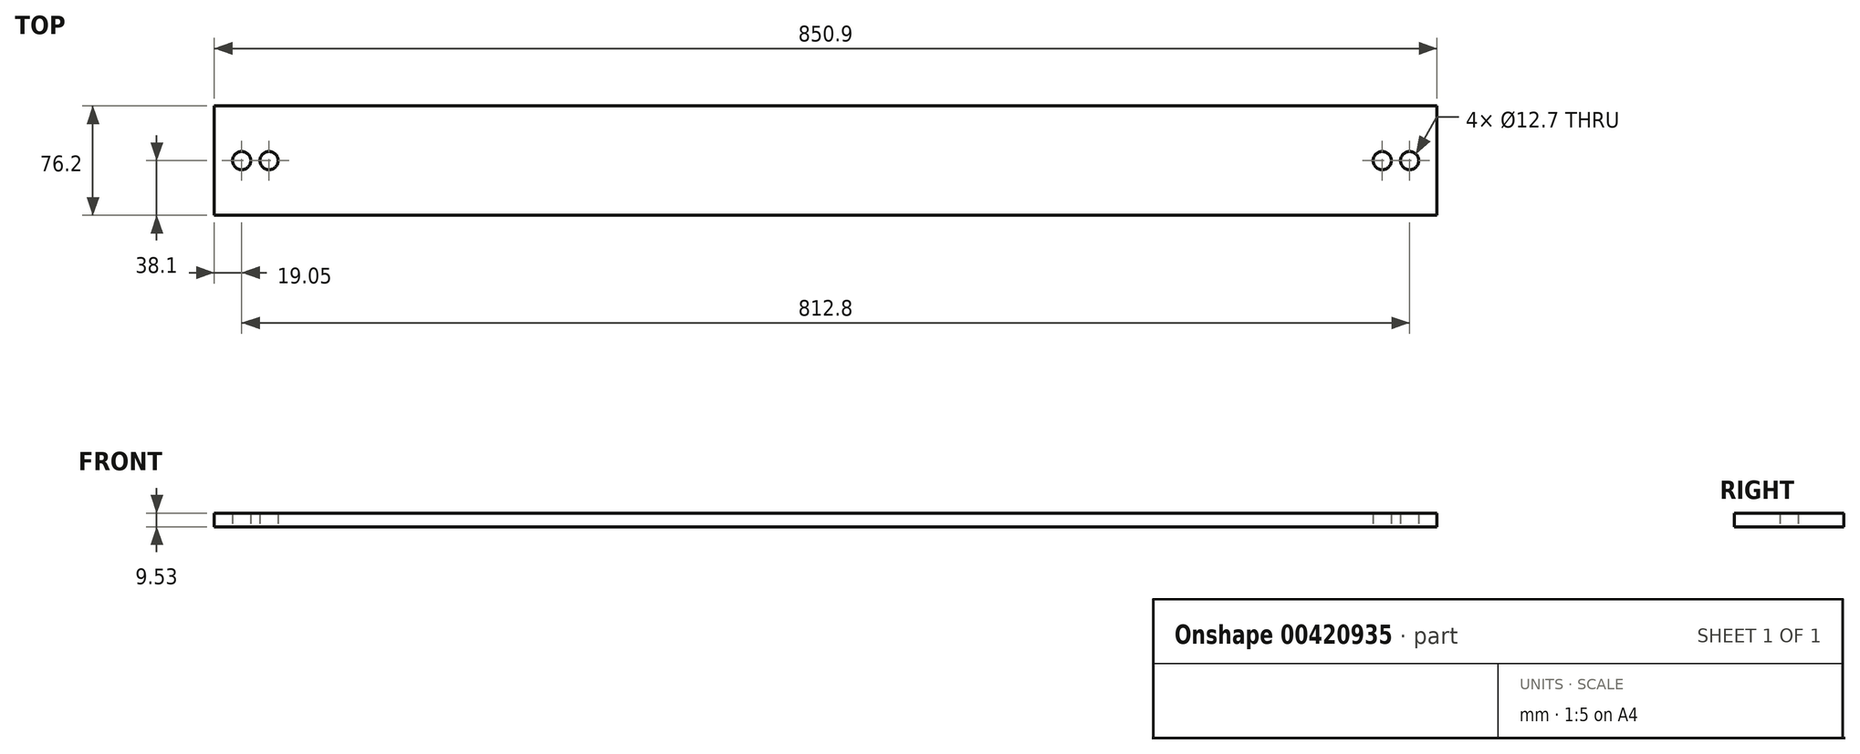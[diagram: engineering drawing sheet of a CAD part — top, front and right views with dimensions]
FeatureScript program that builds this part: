
annotation { "Feature Type Name" : "Feature", "Feature Type Description" : "" }
export const myFeature = defineFeature(function(context is Context, id is Id, definition is map)
    precondition{}
    {
        {
            var Q0;
            Q0=qCreatedBy(makeId("Top.planeOp"),FACE);
            var sketch = newSketch(context, id + "F0", { "sketchPlane" : qUnion([Q0])});
            skLineSegment(sketch, "E0.bottom", {"start": v(0, 0) * mm, "end": v(850.9, 0) * mm});
            skLineSegment(sketch, "E0.top", {"start": v(0, -76.2) * mm, "end": v(850.9, -76.2) * mm});
            skLineSegment(sketch, "E0.left", {"start": v(0, 0) * mm, "end": v(0, -76.2) * mm});
            skLineSegment(sketch, "E0.right", {"start": v(850.9, 0) * mm, "end": v(850.9, -76.2) * mm});
            skCircle(sketch, "E1", {"center": v(19.05, -38.1) * mm, "radius": 6.35 * mm});
            skCircle(sketch, "E2", {"center": v(38.1, -38.1) * mm, "radius": 6.35 * mm});
            skCircle(sketch, "E3", {"center": v(812.8, -38.1) * mm, "radius": 6.35 * mm});
            skCircle(sketch, "E4", {"center": v(831.85, -38.1) * mm, "radius": 6.35 * mm});
            skPoint(sketch, "E5", {"position": v(0, -38.1) * mm});
            skSolve(sketch);
        }
        {
            var Q0;
            Q0=qSketchRegion(id+"F0",true);
            extrude(context, id + "F1", {"entities" : qUnion([Q0]), "depth" : 9.52 * mm});
        }
    });
